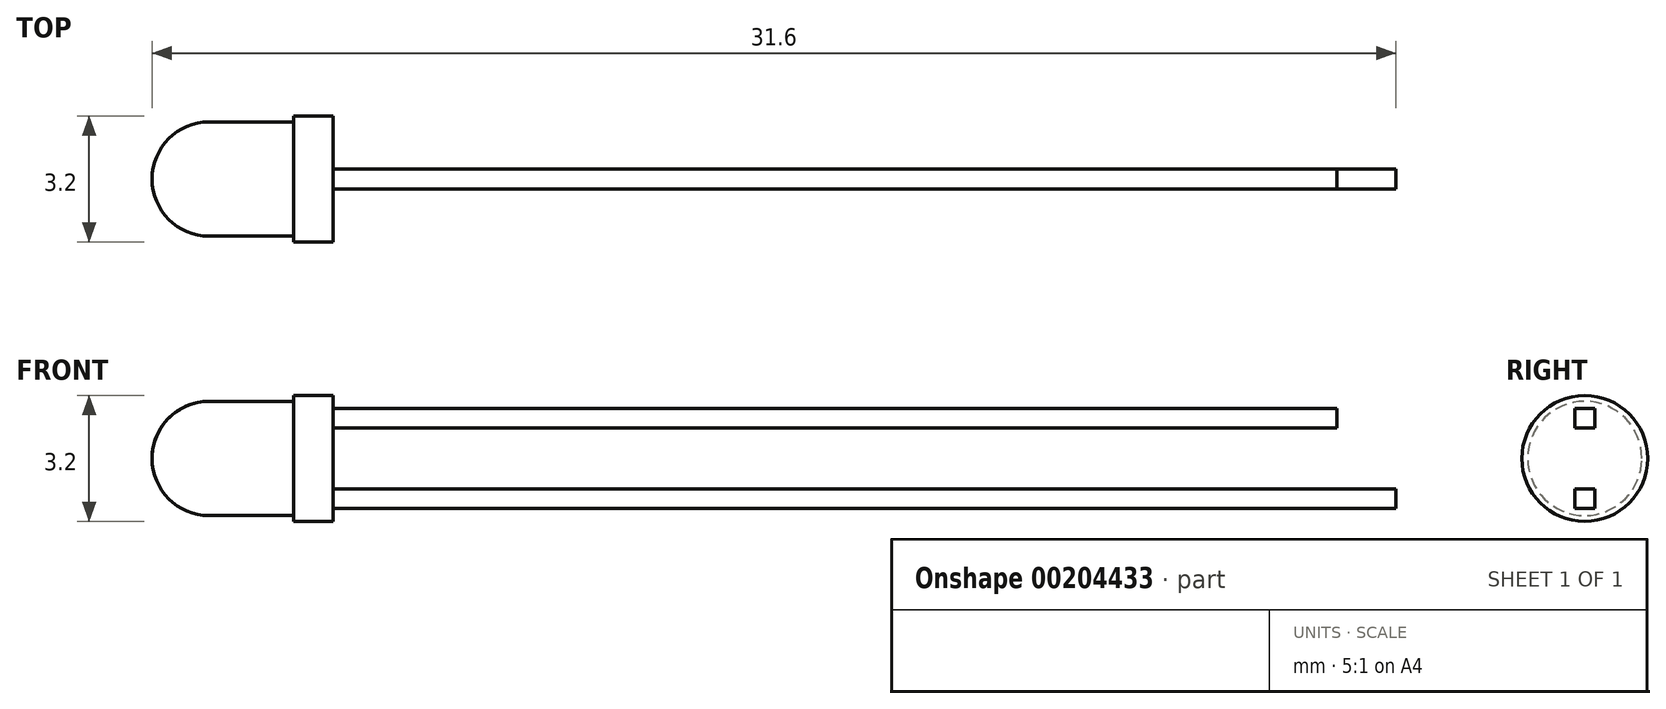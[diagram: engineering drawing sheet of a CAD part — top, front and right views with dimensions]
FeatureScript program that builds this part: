
annotation { "Feature Type Name" : "Feature", "Feature Type Description" : "" }
export const myFeature = defineFeature(function(context is Context, id is Id, definition is map)
    precondition{}
    {
        {
            var Q0;
            Q0=qCreatedBy(makeId("Front.planeOp"),FACE);
            var sketch = newSketch(context, id + "F0", { "sketchPlane" : qUnion([Q0])});
            skArc(sketch, "E0", {"start": v(0, 1.45) * mm, "mid": v(-1.03, 1.03) * mm, "end": v(-1.45, 0) * mm});
            skLineSegment(sketch, "E1", {"start": v(0, 1.45) * mm, "end": v(2.15, 1.45) * mm});
            skLineSegment(sketch, "E2", {"start": v(2.15, 1.45) * mm, "end": v(2.15, 1.6) * mm});
            skLineSegment(sketch, "E3", {"start": v(2.15, 1.6) * mm, "end": v(3.15, 1.6) * mm});
            skLineSegment(sketch, "E4", {"start": v(3.15, 1.6) * mm, "end": v(3.15, 0) * mm});
            skLineSegment(sketch, "E5", {"start": v(-1.45, 0) * mm, "end": v(3.15, 0) * mm});
            skLineSegment(sketch, "E6", {"start": v(3.15, 0) * mm, "end": v(5.51, 0) * mm, "construction": true});
            skSolve(sketch);
        }
        {
            var Q0;
            Q0 = qSketchRegion(id + "F0", true);
            var Q1;
            Q1=sQuery(id+"F0.wireOp",EDGE,"E6");
            revolve(context, id + "F1", {"entities" : qUnion([Q0]), "axis" : qUnion([Q1]), "revolveType" : RevolveType.FULL});
        }
        {
            var Q0;
            Q0=makeQuery(id+"F1.opRevolve","SWEPT_FACE",FACE,{"disambiguationData":[OSD([sQuery(id+"F0.wireOp",EDGE,"E4")])]});
            var sketch = newSketch(context, id + "F2", { "sketchPlane" : qUnion([Q0])});
            skCircle(sketch, "E7", {"center": v(0, 0) * mm, "radius": 1.27 * mm, "construction": true});
            skLineSegment(sketch, "E8", {"start": v(0, 1.27) * mm, "end": v(0, -1.27) * mm, "construction": true});
            skLineSegment(sketch, "E9", {"start": v(-1.27, 0) * mm, "end": v(1.27, 0) * mm, "construction": true});
            skLineSegment(sketch, "E10", {"start": v(0, 1.27) * mm, "end": v(0.25, 1.27) * mm});
            skLineSegment(sketch, "E11", {"start": v(0.25, 1.27) * mm, "end": v(0.25, 0.77) * mm});
            skLineSegment(sketch, "E12", {"start": v(0.25, 0.77) * mm, "end": v(-0.25, 0.77) * mm});
            skLineSegment(sketch, "E13", {"start": v(-0.25, 0.77) * mm, "end": v(-0.25, 1.27) * mm});
            skLineSegment(sketch, "E14", {"start": v(-0.25, 1.27) * mm, "end": v(0, 1.27) * mm});
            skLineSegment(sketch, "E15.MirrorCS", {"start": v(-0.25, -0.77) * mm, "end": v(-0.25, -1.27) * mm});
            skLineSegment(sketch, "E16.MirrorCS", {"start": v(0.25, -0.77) * mm, "end": v(-0.25, -0.77) * mm});
            skLineSegment(sketch, "E17.MirrorCS", {"start": v(-0.25, -1.27) * mm, "end": v(0, -1.27) * mm});
            skLineSegment(sketch, "E18.MirrorCS", {"start": v(0, -1.27) * mm, "end": v(0.25, -1.27) * mm});
            skLineSegment(sketch, "E19.MirrorCS", {"start": v(0.25, -1.27) * mm, "end": v(0.25, -0.77) * mm});
            skSolve(sketch);
        }
        {
            var Q0;
            Q0=makeQuery(id+"F2.imprint","IMPRINT",FACE,{"disambiguationData":[TD([[makeQuery(id+"F2.imprint","IMPRINT",EDGE,{"derivedFrom":sQuery(id+"F2.wireOp",EDGE,"E15.MirrorCS")}),1.0]])]});
            var Q1;
            Q1=makeQuery(id+"F2.imprint","IMPRINT",FACE,{"disambiguationData":[TD([[makeQuery(id+"F2.imprint","IMPRINT",EDGE,{"derivedFrom":sQuery(id+"F2.wireOp",EDGE,"E10")}),-1.0]])]});
            extrude(context, id + "F3", {"entities" : qUnion([Q0, Q1]), "operationType" : NewBodyOperationType.ADD, "depth" : 27 * mm});
        }
        {
            var Q0;
            Q0=makeQuery(id+"F3.opExtrude","CAP_FACE",FACE,{"disambiguationData":[OSD([sQuery(id+"F2.wireOp",EDGE,"E10"),sQuery(id+"F2.wireOp",EDGE,"E11"),sQuery(id+"F2.wireOp",EDGE,"E12"),sQuery(id+"F2.wireOp",EDGE,"E13"),sQuery(id+"F2.wireOp",EDGE,"E14")])],"isStart":false});
            extrude(context, id + "F4", {"entities" : qUnion([Q0]), "operationType" : NewBodyOperationType.REMOVE, "oppositeDirection" : true, "depth" : 1.5 * mm});
        }
    });
